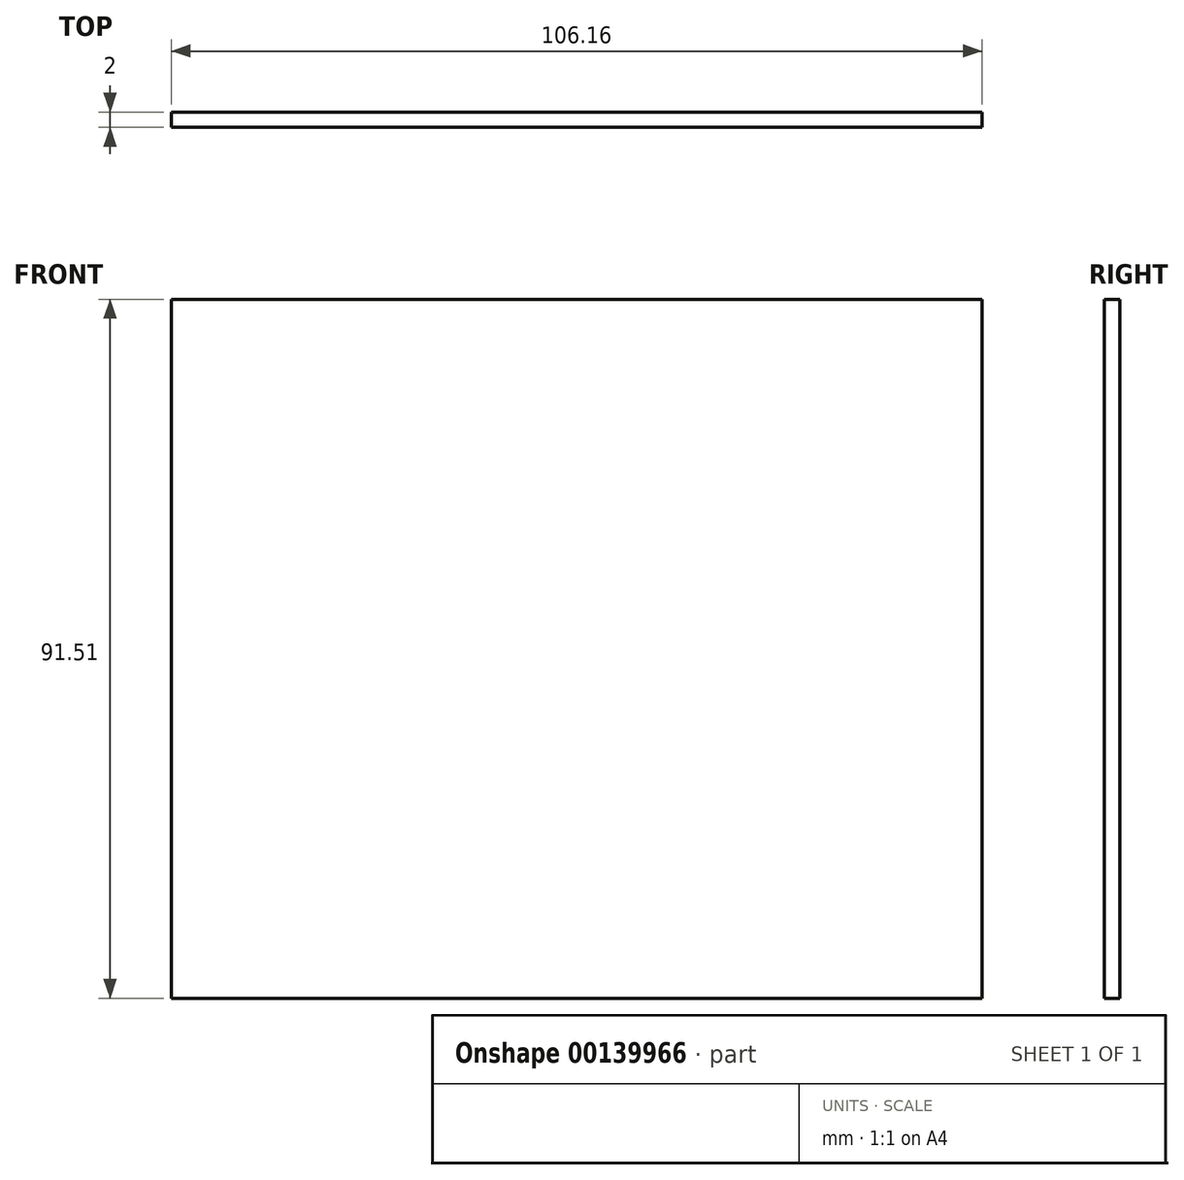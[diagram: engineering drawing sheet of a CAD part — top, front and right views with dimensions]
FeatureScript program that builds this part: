
annotation { "Feature Type Name" : "Feature", "Feature Type Description" : "" }
export const myFeature = defineFeature(function(context is Context, id is Id, definition is map)
    precondition{}
    {
        {
            var Q0;
            Q0=qCreatedBy(makeId("Front.planeOp"),FACE);
            var sketch = newSketch(context, id + "F0", { "sketchPlane" : qUnion([Q0])});
            skLineSegment(sketch, "E0.bottom", {"start": v(-52.78, 53.08) * mm, "end": v(53.38, 53.08) * mm});
            skLineSegment(sketch, "E0.top", {"start": v(-52.78, -38.43) * mm, "end": v(53.38, -38.43) * mm});
            skLineSegment(sketch, "E0.left", {"start": v(-52.78, 53.08) * mm, "end": v(-52.78, -38.43) * mm});
            skLineSegment(sketch, "E0.right", {"start": v(53.38, 53.08) * mm, "end": v(53.38, -38.43) * mm});
            skSolve(sketch);
        }
        {
            var Q0;
            Q0 = qSketchRegion(id + "F0", true);
            extrude(context, id + "F1", {"entities" : qUnion([Q0]), "depth" : 2 * mm});
        }
    });
